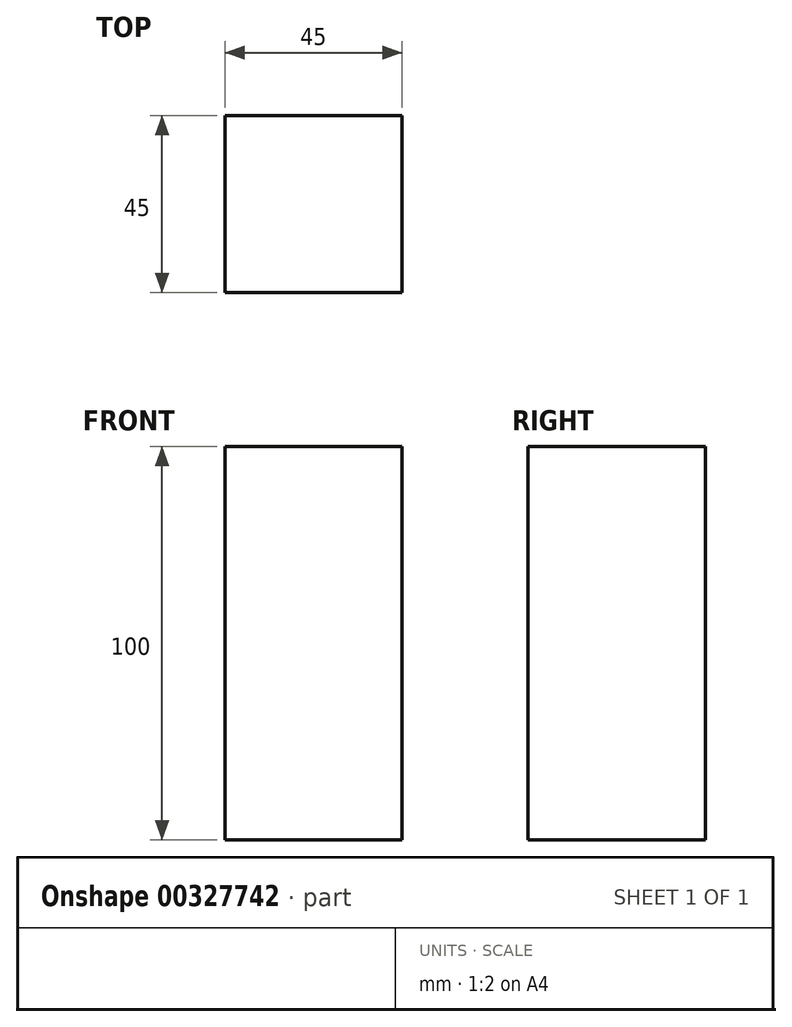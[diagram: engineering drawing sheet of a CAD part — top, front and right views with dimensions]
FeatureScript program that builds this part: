
annotation { "Feature Type Name" : "Feature", "Feature Type Description" : "" }
export const myFeature = defineFeature(function(context is Context, id is Id, definition is map)
    precondition{}
    {
        {
            var Q0;
            Q0=qCreatedBy(makeId("Top.planeOp"),FACE);
            var sketch = newSketch(context, id + "F0", { "sketchPlane" : qUnion([Q0])});
            skLineSegment(sketch, "E0.bottom", {"start": v(22.5, -22.5) * mm, "end": v(-22.5, -22.5) * mm});
            skLineSegment(sketch, "E0.top", {"start": v(22.5, 22.5) * mm, "end": v(-22.5, 22.5) * mm});
            skLineSegment(sketch, "E0.left", {"start": v(22.5, -22.5) * mm, "end": v(22.5, 22.5) * mm});
            skLineSegment(sketch, "E0.right", {"start": v(-22.5, -22.5) * mm, "end": v(-22.5, 22.5) * mm});
            skPoint(sketch, "E0.middle", {"position": v(0, 0) * mm});
            skSolve(sketch);
        }
        {
            var Q0;
            Q0=makeQuery(id+"F0.imprint","IMPRINT",FACE,{"disambiguationData":[TD([[makeQuery(id+"F0.imprint","IMPRINT",EDGE,{"derivedFrom":sQuery(id+"F0.wireOp",EDGE,"E0.bottom")}),-1.0]])]});
            extrude(context, id + "F1", {"entities" : qUnion([Q0]), "depth" : 100 * mm});
        }
    });
